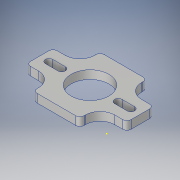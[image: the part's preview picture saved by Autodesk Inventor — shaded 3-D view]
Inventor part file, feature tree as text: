
AUTODESK INVENTOR PART (.ipt)
format: ipt  version: 2018 (Build 220112000, 112)  size: 191,488 bytes
history: native  units: in
note: dims shown in document units (in); Inventor stores cm internally (conversion verified against a paired STEP export)
features: sketch x5, extrude x3, fillet x2, hole x1
ambient origin geometry x8: Origin, YZ Plane, XZ Plane, XY Plane, X Axis, Y Axis, Z Axis, Center Point
bodies: Solid1 (feature_tree)
feature tree (11):
  extrude  "Extrusion1"  Depth=2.0in
  hole  "Hole1"  [1 undecoded]
  extrude  "Extrusion2"  Depth=0.25in
  sketch  "Sketch4"  dims[d13=0.22in d14=0.1875in d15=0.22in d16=0.25in d17=0.0in]
  extrude  "Extrusion3"  Depth=0.25in
  fillet  "Fillet2"  Radius=0.22in
  fillet  "Fillet3"  Radius=0.25in
  sketch  "Sketch1"  dims[d0=3.0in d1=2.0in]
  sketch  "Sketch2"  dims[d2=0.25in d3=0.0in d4=1.125in]
  sketch  "Sketch3"  dims[d5=1.125in d6=0.75in d7=0.375in d8=0.25in d9=0.5635in d10=1.0in d11=0.8108in d12=0.1875in]
  sketch  "Sketch5"  dims[d19=0.6in d20=0.8in d21=0.8in d22=0.6in d23=0.8in d24=1.0in d25=0.0in d26=0.125in d27=0.4375in]
note: 1 required parameter value undecoded (feature->parameter linkage not recoverable at this tier; creation-order binding heuristic only, values carry confidence <= 0.55)
